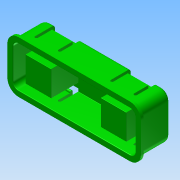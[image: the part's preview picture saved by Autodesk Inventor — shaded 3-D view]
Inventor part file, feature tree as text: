
AUTODESK INVENTOR PART (.ipt)
format: ipt  version: 2015 (Build 190159000, 159)  size: 285,184 bytes
history: native  units: in
note: dims shown in document units (in); Inventor stores cm internally (conversion verified against a paired STEP export)
features: fillet x6, extrude x4, sketch x3, shell x2, plane x2, mirror x2
ambient origin geometry x8: Origin, YZ Plane, XZ Plane, XY Plane, X Axis, Y Axis, Z Axis, Center Point
bodies: Solid1 (feature_tree)
feature tree (19):
  extrude  "Extrusion1"  Depth=0.465in
  fillet  "Fillet1"  Radius=0.57in
  shell  "Shell1"  Thickness=0.2in
  sketch  "Sketch2"  dims[d7=0.46in d8=0.2283in]
  plane  "Work Plane1"
  sketch  "Sketch3"  dims[d9=-0.033in d10=0.47in d11=0.0in d12=0.005in d13=0.01in d14=0.47in d15=0.05in d16=0.1in d17=0.05in d18=0.05in d19=0.15in d20=0.0in d21=0.125in d22=0.0in d23=0.05in d24=0.03in d26=0.445in d27=0.445in d28=0.05in]
  shell  "Shell2"  Thickness=0.1in
  extrude  "Extrusion3"  Depth=0.46in
  plane  "Work Plane2"
  extrude  "Extrusion4"  Depth=0.47in TaperAngle=0.0deg
  fillet  "Fillet6"  Radius=0.005in
  fillet  "Fillet3"  Radius=0.01in
  fillet  "Fillet4"  Radius=0.47in
  extrude  "Extrusion2"  Depth=0.05in
  fillet  "Fillet2"  Radius=0.1in
  fillet  "Fillet7"  Radius=0.05in
  mirror  "Mirror1"
  mirror  "Mirror2"
  sketch  "Sketch1"  dims[d0=1.2in d1=0.465in d2=0.57in d3=0.0in d4=0.2in d5=0.1in]
